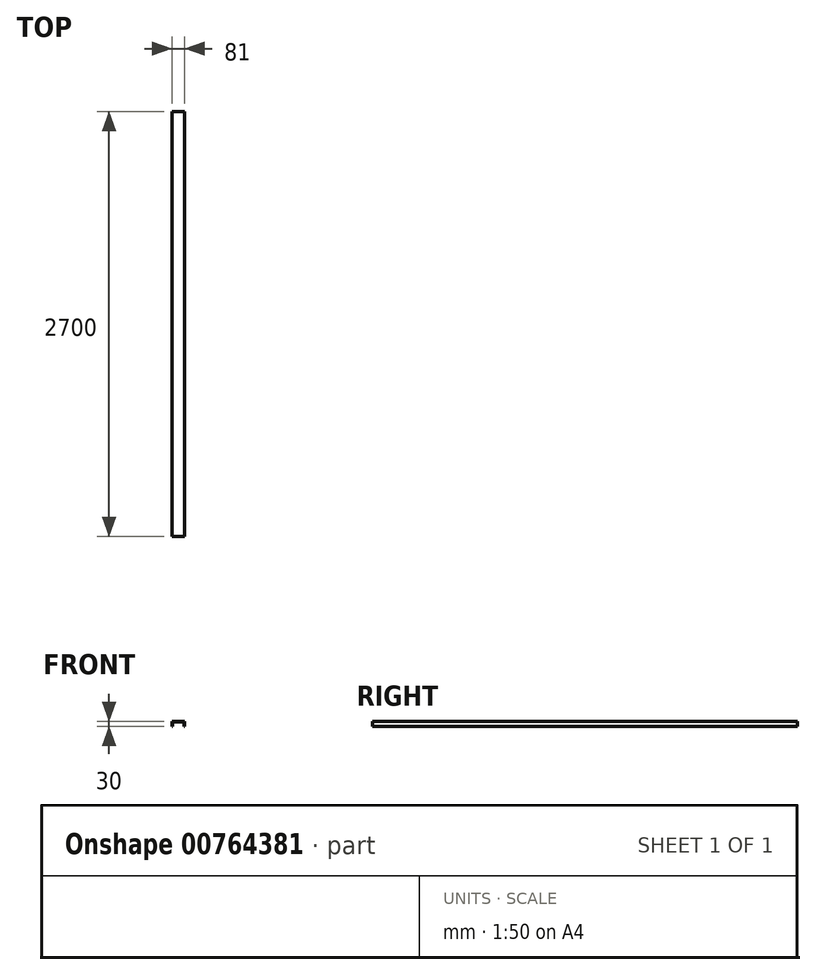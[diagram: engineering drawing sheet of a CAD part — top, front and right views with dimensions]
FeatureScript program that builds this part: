
annotation { "Feature Type Name" : "Feature", "Feature Type Description" : "" }
export const myFeature = defineFeature(function(context is Context, id is Id, definition is map)
    precondition{}
    {
        {
            var Q0;
            Q0=qCreatedBy(makeId("Front.planeOp"),FACE);
            var sketch = newSketch(context, id + "F0", { "sketchPlane" : qUnion([Q0])});
            skLineSegment(sketch, "E0", {"start": v(0, 30) * mm, "end": v(40.5, 30) * mm});
            skLineSegment(sketch, "E1", {"start": v(40.5, 30) * mm, "end": v(40.5, 0) * mm});
            skLineSegment(sketch, "E2", {"start": v(0, 30) * mm, "end": v(-40.5, 30) * mm});
            skLineSegment(sketch, "E3", {"start": v(-40.5, 30) * mm, "end": v(-40.5, 0) * mm});
            skLineSegment(sketch, "E4.0", {"start": v(-37.5, 27) * mm, "end": v(-37.5, 0) * mm});
            skLineSegment(sketch, "E4.1", {"start": v(0, 27) * mm, "end": v(-37.5, 27) * mm});
            skLineSegment(sketch, "E4.2", {"start": v(0, 27) * mm, "end": v(37.5, 27) * mm});
            skLineSegment(sketch, "E4.3", {"start": v(37.5, 27) * mm, "end": v(37.5, 0) * mm});
            skLineSegment(sketch, "E5", {"start": v(-40.5, 0) * mm, "end": v(-37.5, 0) * mm});
            skLineSegment(sketch, "E6", {"start": v(37.5, 0) * mm, "end": v(40.5, 0) * mm});
            skSolve(sketch);
        }
        {
            var Q0;
            Q0=makeQuery(id+"F0.imprint","IMPRINT",FACE,{"disambiguationData":[TD([[makeQuery(id+"F0.imprint","IMPRINT",EDGE,{"derivedFrom":sQuery(id+"F0.wireOp",EDGE,"E0")}),-1.0]])]});
            extrude(context, id + "F1", {"entities" : qUnion([Q0]), "depth" : 2700 * mm, "offsetDistance" : 25 * mm, "symmetric" : true});
        }
    });
